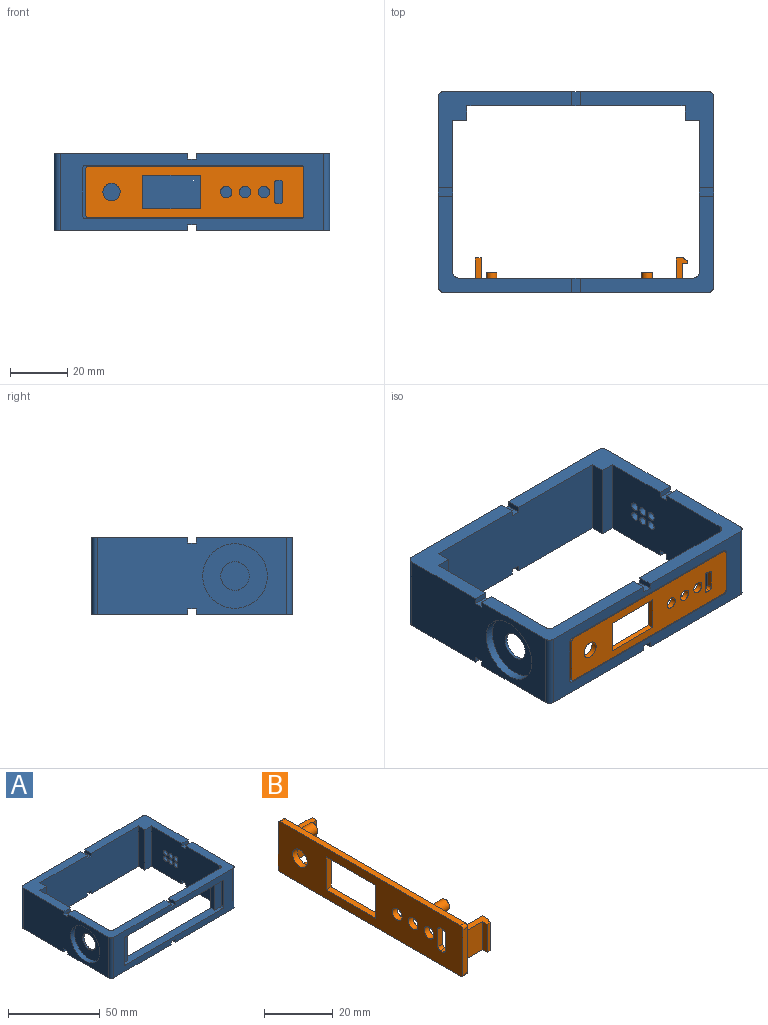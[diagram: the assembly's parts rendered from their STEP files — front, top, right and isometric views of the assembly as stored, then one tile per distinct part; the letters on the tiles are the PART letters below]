
ASSEMBLY  parts=2 mates=1
PART A: 75 faces, bbox 96x70x27 mm
  f0: plane 53x27mm, normal (1,0,0), area 1081.1mm2, adj f7,f10,f11,f17,f44,f45,f53,f54
  f1: cylinder r=5mm len=10mm, axis (-1,0,0), area 31.4mm2, adj f32,f74
  f2: plane 76x27mm, normal (0,-1,0), area 2040mm2, adj f5,f9,f10,f15,f16,f44,f47,f48
  f3: plane 66x27mm, normal (1,0,0), area 1727.6mm2, adj f5,f6,f8,f9,f21,f22,f25,f26
  f4: plane 92x27mm, normal (0,1,0), area 2472mm2, adj f5,f9,f10,f22,f23,f44,f47,f48
  f5: plane 46.5x33.5mm, normal (0,0,-1), area 399.1mm2, adj f2,f3,f4,f13,f14,f15,f22,f66
  f6: plane 46.5x33.5mm, normal (0,0,-1), area 375mm2, adj f3,f12,f13,f18,f21,f46,f62,f65
  f7: plane 46.5x33.5mm, normal (0,0,-1), area 375mm2, adj f0,f12,f18,f19,f20,f45,f59,f63
  f8: plane 46.5x33.5mm, normal (0,0,1), area 375mm2, adj f3,f12,f13,f18,f21,f46,f51,f56
  f9: plane 46.5x33.5mm, normal (0,0,1), area 399.1mm2, adj f2,f3,f4,f13,f14,f15,f22,f47
  f10: plane 46.5x33.5mm, normal (0,0,1), area 399.1mm2, adj f0,f2,f4,f16,f17,f19,f23,f48
  f11: plane 46.5x33.5mm, normal (0,0,1), area 375mm2, adj f0,f12,f18,f19,f20,f45,f54,f57
  f12: plane 82x27mm, normal (0,1,0), area 945.7mm2, adj f6,f7,f8,f11,f33,f37,f42,f43
  f13: plane 53x27mm, normal (-1,0,0), area 1376.6mm2, adj f5,f6,f8,f9,f14,f25,f26,f27
  f14: plane 27x5mm, normal (0,-1,0), area 135mm2, adj f5,f9,f13,f15
  f15: plane 27x5mm, normal (-1,0,0), area 135mm2, adj f2,f5,f9,f14
  f16: plane 27x5mm, normal (1,0,0), area 135mm2, adj f2,f10,f17,f44
  f17: plane 27x5mm, normal (0,-1,0), area 135mm2, adj f0,f10,f16,f44
  f18: plane 92x27mm, normal (0,-1,0), area 1029.1mm2, adj f6,f7,f8,f11,f20,f21,f33,f34
  f19: plane 66x27mm, normal (-1,0,0), area 1372.4mm2, adj f7,f10,f11,f20,f23,f31,f44,f53
  f20: cylinder r=2mm len=27mm, axis (0,0,-1), area 84.8mm2, adj f7,f11,f18,f19
  f21: cylinder r=2mm len=27mm, axis (0,0,-1), area 84.8mm2, adj f3,f6,f8,f18
  f22: cylinder r=2mm len=27mm, axis (0,0,-1), area 84.8mm2, adj f3,f4,f5,f9
  f23: cylinder r=2mm len=27mm, axis (0,0,-1), area 84.8mm2, adj f4,f10,f19,f44
  f24: plane 18.75x5mm, normal (0,-1,0), area 93.3mm2, adj f33,f34,f35,f36,f37,f43
  f25: cylinder r=1.5mm len=5mm, axis (1,0,0), area 47.1mm2, adj f3,f13
  f26: cylinder r=1.5mm len=5mm, axis (1,0,0), area 47.1mm2, adj f3,f13
  f27: cylinder r=1.5mm len=5mm, axis (1,0,0), area 47.1mm2, adj f3,f13
  f28: cylinder r=1.5mm len=5mm, axis (1,0,0), area 47.1mm2, adj f3,f13
  f29: cylinder r=1.5mm len=5mm, axis (1,0,0), area 47.1mm2, adj f3,f13
  f30: cylinder r=1.5mm len=5mm, axis (1,0,0), area 47.1mm2, adj f3,f13
  f31: cylinder r=11.25mm len=22.5mm, axis (-1,0,0), area 212.1mm2, adj f19,f32
  f32: plane 22.5x22.5mm, normal (-1,0,0), area 319.1mm2, adj f1,f31
  f33: plane 75x5mm, normal (0,0,1), area 351mm2, adj f12,f18,f24,f34,f40,f41,f42,f43
  f34: cylinder r=1mm len=2mm, axis (0,-1,0), area 3.1mm2, adj f18,f24,f33,f35
  f35: plane 16.75x2mm, normal (-1,0,0), area 33.5mm2, adj f18,f24,f34,f36
  f36: cylinder r=1mm len=2mm, axis (0,-1,0), area 3.1mm2, adj f18,f24,f35,f37
  f37: plane 75x5mm, normal (0,0,-1), area 351mm2, adj f12,f18,f24,f36,f38,f41,f42,f43
  f38: cylinder r=1mm len=2mm, axis (0,-1,0), area 3.1mm2, adj f18,f37,f39,f41
  f39: plane 16.75x2mm, normal (1,0,0), area 33.5mm2, adj f18,f38,f40,f41
  f40: cylinder r=1mm len=2mm, axis (0,-1,0), area 3.1mm2, adj f18,f33,f39,f41
  f41: plane 18.75x5mm, normal (0,-1,0), area 93.3mm2, adj f33,f37,f38,f39,f40,f42
  f42: plane 18.75x3mm, normal (1,0,0), area 56.3mm2, adj f12,f33,f37,f41
  f43: plane 18.75x3mm, normal (-1,0,0), area 56.3mm2, adj f12,f24,f33,f37
  f44: plane 46.5x33.5mm, normal (0,0,-1), area 399.1mm2, adj f0,f2,f4,f16,f17,f19,f23,f60
  f45: cylinder r=2mm len=27mm, axis (0,0,1), area 84.8mm2, adj f0,f7,f11,f12
  f46: cylinder r=2mm len=27mm, axis (0,0,-1), area 84.8mm2, adj f6,f8,f12,f13
  f47: plane 5x2mm, normal (-1,0,0), area 10mm2, adj f2,f4,f9,f49
  f48: plane 5x2mm, normal (1,0,0), area 10mm2, adj f2,f4,f10,f49
  f49: plane 5x3mm, normal (0,0,1), area 15mm2, adj f2,f4,f47,f48
  f50: plane 5x2mm, normal (0,-1,0), area 10mm2, adj f3,f9,f13,f52
  f51: plane 5x2mm, normal (0,1,0), area 10mm2, adj f3,f8,f13,f52
  f52: plane 5x3mm, normal (0,0,1), area 15mm2, adj f3,f13,f50,f51
  f53: plane 5x2mm, normal (0,-1,0), area 10mm2, adj f0,f10,f19,f55
  f54: plane 5x2mm, normal (0,1,0), area 10mm2, adj f0,f11,f19,f55
  f55: plane 5x3mm, normal (0,0,1), area 15mm2, adj f0,f19,f53,f54
  f56: plane 5x2mm, normal (-1,0,0), area 10mm2, adj f8,f12,f18,f58
  f57: plane 5x2mm, normal (1,0,0), area 10mm2, adj f11,f12,f18,f58
  f58: plane 5x3mm, normal (0,0,1), area 15mm2, adj f12,f18,f56,f57
  f59: plane 5x2mm, normal (0,1,0), area 10mm2, adj f0,f7,f19,f61
  f60: plane 5x2mm, normal (0,-1,0), area 10mm2, adj f0,f19,f44,f61
  f61: plane 5x3mm, normal (0,0,-1), area 15mm2, adj f0,f19,f59,f60
  f62: plane 5x2mm, normal (-1,0,0), area 10mm2, adj f6,f12,f18,f64
  f63: plane 5x2mm, normal (1,0,0), area 10mm2, adj f7,f12,f18,f64
  f64: plane 5x3mm, normal (0,0,-1), area 15mm2, adj f12,f18,f62,f63
  f65: plane 5x2mm, normal (0,1,0), area 10mm2, adj f3,f6,f13,f67
  f66: plane 5x2mm, normal (0,-1,0), area 10mm2, adj f3,f5,f13,f67
  f67: plane 5x3mm, normal (0,0,-1), area 15mm2, adj f3,f13,f65,f66
  f68: plane 5x2mm, normal (-1,0,0), area 10mm2, adj f2,f4,f5,f70
  f69: plane 5x2mm, normal (1,0,0), area 10mm2, adj f2,f4,f44,f70
  f70: plane 5x3mm, normal (0,0,-1), area 15mm2, adj f2,f4,f68,f69
  f71: plane 12x6.93mm, normal (0,-0.5,-0.87), area 13.9mm2, adj f0,f72,f73,f74
  f72: cylinder r=9.5mm len=19mm, axis (1,0,0), area 44.2mm2, adj f0,f71,f73,f74
  f73: plane 12x6.93mm, normal (0,-0.5,0.87), area 13.9mm2, adj f0,f71,f72,f74
  f74: plane 28x19mm, normal (1,0,0), area 259.4mm2, adj f1,f71,f72,f73
PART B: 51 faces, bbox 16.1x79.1x18.1 mm
  f0: plane 10x8mm, normal (0,-1,0), area 80mm2, adj f1,f39,f41,f48
  f1: plane 76x18mm, normal (1,0,0), area 970.6mm2, adj f0,f2,f3,f4,f5,f6,f7,f8
  f2: plane 74x2mm, normal (0,0,-1), area 148mm2, adj f1,f20,f36,f37
  f3: plane 74x2mm, normal (0,0,1), area 148mm2, adj f1,f20,f35,f38
  f4: cylinder r=1mm len=2mm, axis (-1,0,0), area 3.1mm2, adj f1,f5,f14,f20
  f5: plane 2x1mm, normal (0,0,1), area 2mm2, adj f1,f4,f6,f20
  f6: cylinder r=1mm len=2mm, axis (-1,0,0), area 3.1mm2, adj f1,f5,f7,f20
  f7: plane 6.2x2mm, normal (0,1,0), area 12.4mm2, adj f1,f6,f8,f20
  f8: cylinder r=1mm len=2mm, axis (-1,0,0), area 3.1mm2, adj f1,f7,f9,f20
  f9: plane 2x1mm, normal (0,0,-1), area 2mm2, adj f1,f8,f10,f20
  f10: cylinder r=1mm len=2mm, axis (-1,0,0), area 3.1mm2, adj f1,f9,f14,f20
  f11: plane 11.72x2mm, normal (0,1,0), area 23.4mm2, adj f1,f12,f15,f20
  f12: plane 20.16x2mm, normal (0,0,-1), area 40.3mm2, adj f1,f11,f13,f20
  f13: plane 11.72x2mm, normal (0,-1,0), area 23.4mm2, adj f1,f12,f15,f20
  f14: plane 6.2x2mm, normal (0,-1,0), area 12.4mm2, adj f1,f4,f10,f20
  f15: plane 20.16x2mm, normal (0,0,1), area 40.3mm2, adj f1,f11,f13,f20
  f16: cylinder r=2mm len=4mm, axis (-1,0,0), area 25.1mm2, adj f1,f20
  f17: cylinder r=2mm len=4mm, axis (-1,0,0), area 25.1mm2, adj f1,f20
  f18: cylinder r=2mm len=4mm, axis (-1,0,0), area 25.1mm2, adj f1,f20
  f19: cylinder r=3mm len=6mm, axis (-1,0,0), area 37.7mm2, adj f1,f20
  f20: plane 76x18mm, normal (-1,0,0), area 1041.2mm2, adj f2,f3,f4,f5,f6,f7,f8,f9
  f21: cylinder r=1.8mm len=4.9mm, axis (-1,0,0), area 55.4mm2, adj f1,f23
  f22: cylinder r=0.8mm len=5.9mm, axis (-1,0,0), area 29.7mm2, adj f23,f31
  f23: plane 3.6x3.6mm, normal (1,0,0), area 8.2mm2, adj f21,f22
  f24: cylinder r=1.8mm len=4.9mm, axis (-1,0,0), area 55.4mm2, adj f1,f26
  f25: cylinder r=0.8mm len=5.9mm, axis (-1,0,0), area 29.7mm2, adj f26,f32
  f26: plane 3.6x3.6mm, normal (1,0,0), area 8.2mm2, adj f24,f25
  f27: cylinder r=1.8mm len=4.9mm, axis (-1,0,0), area 55.4mm2, adj f1,f29
  f28: cylinder r=0.8mm len=5.9mm, axis (-1,0,0), area 29.7mm2, adj f29,f30
  f29: plane 3.6x3.6mm, normal (1,0,0), area 8.2mm2, adj f27,f28
  f30: plane 1.6x1.6mm, normal (1,0,0), area 2mm2, adj f28
  f31: plane 1.6x1.6mm, normal (1,0,0), area 2mm2, adj f22
  f32: plane 1.6x1.6mm, normal (1,0,0), area 2mm2, adj f25
  f33: plane 16x2mm, normal (0,-1,0), area 32mm2, adj f1,f20,f37,f38
  f34: plane 16x2mm, normal (0,1,0), area 32mm2, adj f1,f20,f35,f36
  f35: cylinder r=1mm len=2mm, axis (-1,0,0), area 3.1mm2, adj f1,f3,f20,f34
  f36: cylinder r=1mm len=2mm, axis (1,0,0), area 3.1mm2, adj f1,f2,f20,f34
  f37: cylinder r=1mm len=2mm, axis (-1,0,0), area 3.1mm2, adj f1,f2,f20,f33
  f38: cylinder r=1mm len=2mm, axis (1,0,0), area 3.1mm2, adj f1,f3,f20,f33
  f39: plane 10.09x4.09mm, normal (0,0,-1), area 23.2mm2, adj f0,f1,f40,f42,f48,f49,f50
  f40: plane 10x10mm, normal (0,1,0), area 100mm2, adj f1,f39,f41,f42
  f41: plane 10.1x4.1mm, normal (0,0,1), area 23.2mm2, adj f0,f1,f40,f42,f48,f49,f50
  f42: plane 10x2.54mm, normal (1,0,0), area 25.4mm2, adj f39,f40,f41,f50
  f43: plane 10x2mm, normal (0,0,-1), area 20mm2, adj f1,f44,f46,f47
  f44: plane 10x10mm, normal (0,1,0), area 100mm2, adj f1,f43,f45,f47
  f45: plane 10x2mm, normal (0,0,1), area 20mm2, adj f1,f44,f46,f47
  f46: plane 10x10mm, normal (0,-1,0), area 100mm2, adj f1,f43,f45,f47
  f47: plane 10x2mm, normal (1,0,0), area 20mm2, adj f43,f44,f45,f46
  f48: plane 10x2mm, normal (-1,0,0), area 20mm2, adj f0,f39,f41,f49
  f49: plane 10x1.15mm, normal (0,-1,0), area 11.5mm2, adj f39,f41,f48,f50
  f50: bspline ~11x5mm, area 17.3mm2, adj f39,f41,f42,f49
PLACE A t=(11.27,17.79,2.85)mm
PLACE B rot(axis=(0,0,1),90deg) t=(19.34,-17.21,17.27)mm
MATE fastened B.f1 <-> A.f24  axis (0,1,0) through (50.22,-15.21,16.92)mm
